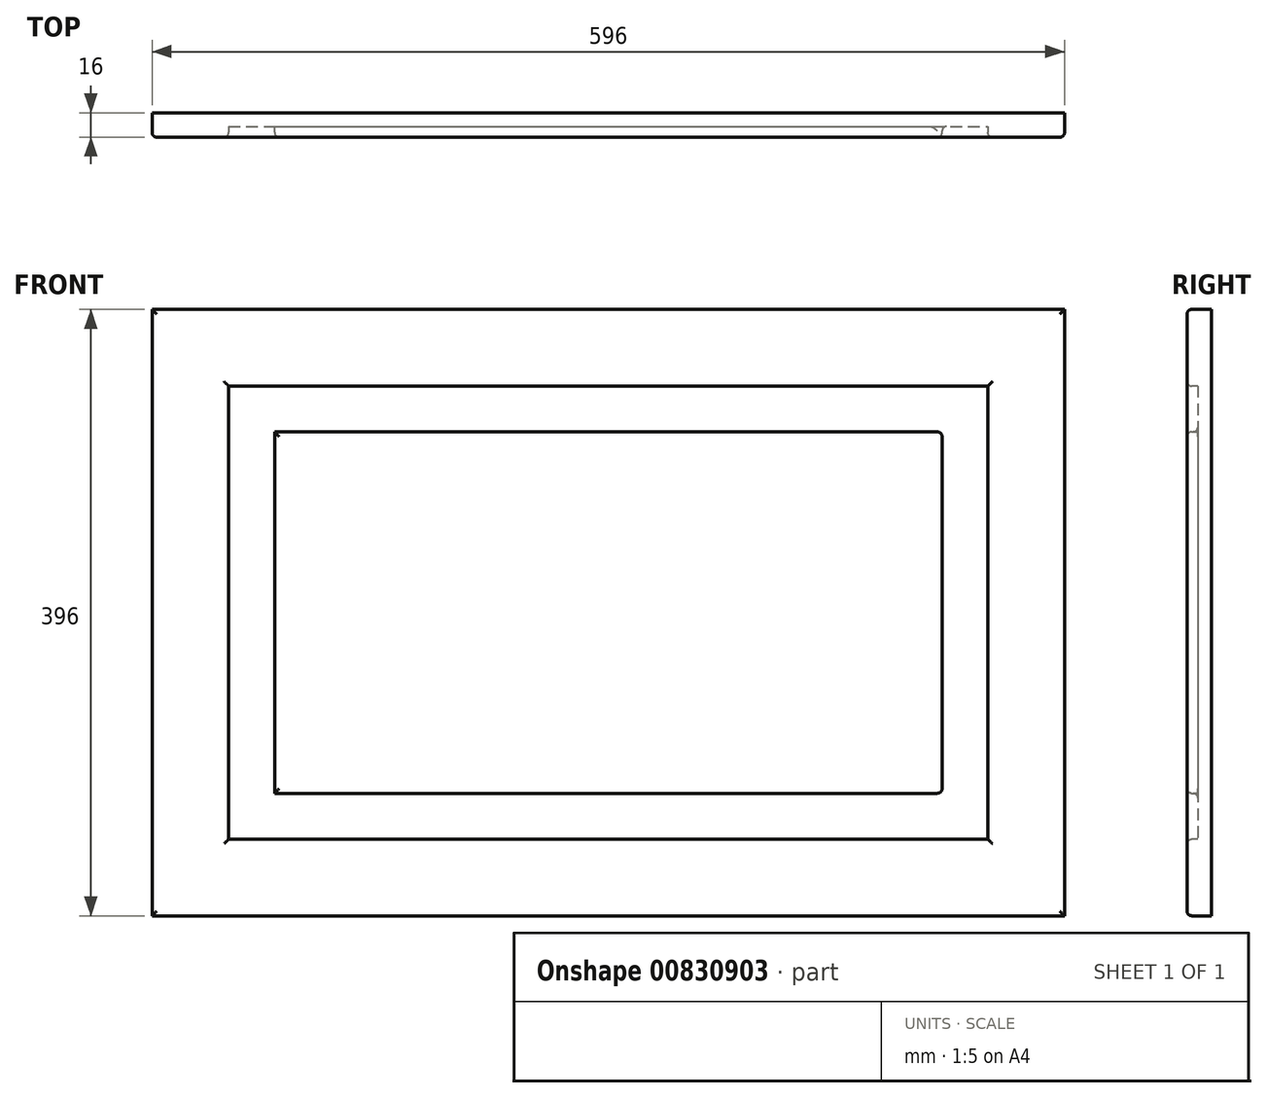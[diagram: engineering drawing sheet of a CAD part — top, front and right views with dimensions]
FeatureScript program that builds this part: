
annotation { "Feature Type Name" : "Feature", "Feature Type Description" : "" }
export const myFeature = defineFeature(function(context is Context, id is Id, definition is map)
    precondition{}
    {
        {
            var Q0;
            Q0=qCreatedBy(makeId("Front.planeOp"),FACE);
            var sketch = newSketch(context, id + "F0", { "sketchPlane" : qUnion([Q0])});
            skLineSegment(sketch, "E0.bottom", {"start": v(0, 0) * mm, "end": v(44.66, 0) * mm});
            skLineSegment(sketch, "E0.top", {"start": v(0, 33.8) * mm, "end": v(44.66, 33.8) * mm});
            skLineSegment(sketch, "E0.left", {"start": v(0, 0) * mm, "end": v(0, 33.8) * mm});
            skLineSegment(sketch, "E0.right", {"start": v(44.66, 0) * mm, "end": v(44.66, 33.8) * mm});
            skSolve(sketch);
        }
        {
            var Q0;
            Q0=makeQuery(id+"F0.imprint","IMPRINT",FACE,{"disambiguationData":[TD([[makeQuery(id+"F0.imprint","IMPRINT",EDGE,{"derivedFrom":sQuery(id+"F0.wireOp",EDGE,"E0.bottom")}),1.0]])]});
            extrude(context, id + "F1", {"entities" : qUnion([Q0]), "depth" : 16 * mm, "offsetDistance" : 25.4 * mm});
        }
        {
            var Q0;
            Q0=makeQuery(id+"F1.opExtrude","SWEPT_FACE",FACE,{"disambiguationData":[OSD([sQuery(id+"F0.wireOp",EDGE,"E0.bottom")])]});
            extrude(context, id + "F2", {"entities" : qUnion([Q0]), "operationType" : NewBodyOperationType.ADD, "oppositeDirection" : true, "depth" : 796 * mm, "offsetDistance" : 25 * mm});
        }
        {
            var Q0;
            {var subQ0=sQuery(id+"F0.wireOp",EDGE,"E0.left");Q0=makeQuery(id+"F2.boolean.opBoolean","MERGE",FACE,{"derivedFrom":[makeQuery(id+"F1.opExtrude","SWEPT_FACE",FACE,{"disambiguationData":[OSD([subQ0])]}),makeQuery(id+"F2.opExtrude","SWEPT_FACE",FACE,{"disambiguationData":[OSD([sQuery(id+"F0.wireOp",EDGE,"E0.bottom"),subQ0])]})]});}
            extrude(context, id + "F3", {"entities" : qUnion([Q0]), "operationType" : NewBodyOperationType.ADD, "oppositeDirection" : true, "depth" : 196 * mm, "offsetDistance" : 25 * mm});
        }
        {
            var Q0;
            {var subQ0=sQuery(id+"F0.wireOp",EDGE,"E0.left");var subQ1=sQuery(id+"F0.wireOp",EDGE,"E0.bottom");Q0=makeQuery(id+"F3.boolean.opBoolean","MERGE",FACE,{"derivedFrom":[makeQuery(id+"F2.boolean.opBoolean","MERGE",FACE,{"derivedFrom":[makeQuery(id+"F1.opExtrude","CAP_FACE",FACE,{"disambiguationData":[OSD([subQ1,sQuery(id+"F0.wireOp",EDGE,"E0.top"),subQ0,sQuery(id+"F0.wireOp",EDGE,"E0.right")])],"isStart":false}),makeQuery(id+"F2.opExtrude","SWEPT_FACE",FACE,{"disambiguationData":[OSD([subQ1]),TDD([makeQuery(id+"F1.opExtrude","CAP_EDGE",EDGE,{"disambiguationData":[OSD([subQ1])],"isStart":false})])]})]}),makeQuery(id+"F3.opExtrude","SWEPT_FACE",FACE,{"disambiguationData":[OSD([subQ1,subQ0]),TDD([makeQuery(id+"F2.boolean.opBoolean","MERGE",EDGE,{"derivedFrom":[makeQuery(id+"F1.opExtrude","CAP_EDGE",EDGE,{"disambiguationData":[OSD([subQ0])],"isStart":false}),makeQuery(id+"F2.opExtrude","SWEPT_EDGE",EDGE,{"disambiguationData":[OSD([subQ1,subQ0]),TDD([makeQuery(id+"F1.opExtrude","CAP_VERTEX",VERTEX,{"disambiguationData":[OSD([subQ1,subQ0])],"isStart":false})])]})]})])]})]});}
            var sketch = newSketch(context, id + "F4", { "sketchPlane" : qUnion([Q0])});
            skLineSegment(sketch, "E1.bottom", {"start": v(59.7, 646.67) * mm, "end": v(128.66, 646.67) * mm});
            skLineSegment(sketch, "E1.top", {"start": v(59.7, 152.97) * mm, "end": v(128.66, 152.97) * mm});
            skLineSegment(sketch, "E1.left", {"start": v(59.7, 646.67) * mm, "end": v(59.7, 152.97) * mm});
            skLineSegment(sketch, "E1.right", {"start": v(128.66, 646.67) * mm, "end": v(128.66, 152.97) * mm});
            skSolve(sketch);
        }
        {
            var Q0;
            Q0=makeQuery(id+"F4.imprint","IMPRINT",FACE,{"disambiguationData":[TD([[makeQuery(id+"F4.imprint","IMPRINT",EDGE,{"derivedFrom":sQuery(id+"F4.wireOp",EDGE,"E1.bottom")}),-1.0]])]});
            extrude(context, id + "F5", {"entities" : qUnion([Q0]), "operationType" : NewBodyOperationType.REMOVE, "oppositeDirection" : true, "depth" : 7 * mm, "offsetDistance" : 25 * mm});
        }
        {
            var Q0;
            Q0=makeQuery(id+"F5.boolean.opBoolean","COPY",FACE,{"derivedFrom":makeQuery(id+"F5.opExtrude","SWEPT_FACE",FACE,{"disambiguationData":[OSD([sQuery(id+"F4.wireOp",EDGE,"E1.left")])]})});
            extrude(context, id + "F6", {"entities" : qUnion([Q0]), "operationType" : NewBodyOperationType.REMOVE, "oppositeDirection" : true, "depth" : 9.7 * mm, "offsetDistance" : 25 * mm});
        }
        {
            var Q0;
            {var subQ0=sQuery(id+"F4.wireOp",EDGE,"E1.bottom");Q0=makeQuery(id+"F6.boolean.opBoolean","MERGE",FACE,{"derivedFrom":[makeQuery(id+"F5.boolean.opBoolean","COPY",FACE,{"derivedFrom":makeQuery(id+"F5.opExtrude","SWEPT_FACE",FACE,{"disambiguationData":[OSD([subQ0])]})}),makeQuery(id+"F6.opExtrude","SWEPT_FACE",FACE,{"disambiguationData":[OSD([subQ0,sQuery(id+"F4.wireOp",EDGE,"E1.left")])]})]});}
            extrude(context, id + "F7", {"entities" : qUnion([Q0]), "operationType" : NewBodyOperationType.ADD, "oppositeDirection" : true, "depth" : 99.33 * mm, "offsetDistance" : 25 * mm});
        }
        {
            var Q0;
            {var subQ0=sQuery(id+"F4.wireOp",EDGE,"E1.bottom");Q0=makeQuery(id+"F6.boolean.opBoolean","MERGE",FACE,{"derivedFrom":[makeQuery(id+"F5.boolean.opBoolean","COPY",FACE,{"derivedFrom":makeQuery(id+"F5.opExtrude","SWEPT_FACE",FACE,{"disambiguationData":[OSD([subQ0])]})}),makeQuery(id+"F6.opExtrude","SWEPT_FACE",FACE,{"disambiguationData":[OSD([subQ0,sQuery(id+"F4.wireOp",EDGE,"E1.left")])]})]});}
            extrude(context, id + "F8", {"entities" : qUnion([Q0]), "operationType" : NewBodyOperationType.REMOVE, "oppositeDirection" : true, "depth" : 99.33 * mm, "offsetDistance" : 25 * mm});
        }
        {
            var Q0;
            {var subQ0=sQuery(id+"F4.wireOp",EDGE,"E1.right");Q0=makeQuery(id+"F8.boolean.opBoolean","MERGE",FACE,{"derivedFrom":[makeQuery(id+"F5.boolean.opBoolean","COPY",FACE,{"derivedFrom":makeQuery(id+"F5.opExtrude","SWEPT_FACE",FACE,{"disambiguationData":[OSD([subQ0])]})}),makeQuery(id+"F8.opExtrude","SWEPT_FACE",FACE,{"disambiguationData":[OSD([sQuery(id+"F4.wireOp",EDGE,"E1.bottom"),subQ0])]})]});}
            extrude(context, id + "F9", {"entities" : qUnion([Q0]), "operationType" : NewBodyOperationType.REMOVE, "oppositeDirection" : true, "depth" : 17.34 * mm, "offsetDistance" : 25 * mm});
        }
        {
            var Q0;
            {var subQ0=sQuery(id+"F4.wireOp",EDGE,"E1.top");Q0=makeQuery(id+"F9.boolean.opBoolean","MERGE",FACE,{"derivedFrom":[makeQuery(id+"F6.boolean.opBoolean","MERGE",FACE,{"derivedFrom":[makeQuery(id+"F5.boolean.opBoolean","COPY",FACE,{"derivedFrom":makeQuery(id+"F5.opExtrude","SWEPT_FACE",FACE,{"disambiguationData":[OSD([subQ0])]})}),makeQuery(id+"F6.opExtrude","SWEPT_FACE",FACE,{"disambiguationData":[OSD([subQ0,sQuery(id+"F4.wireOp",EDGE,"E1.left")])]})]}),makeQuery(id+"F9.opExtrude","SWEPT_FACE",FACE,{"disambiguationData":[OSD([subQ0,sQuery(id+"F4.wireOp",EDGE,"E1.right")])]})]});}
            extrude(context, id + "F10", {"entities" : qUnion([Q0]), "operationType" : NewBodyOperationType.REMOVE, "oppositeDirection" : true, "depth" : 102.97 * mm, "offsetDistance" : 25 * mm});
        }
        {
            var Q0;
            {var subQ0=sQuery(id+"F4.wireOp",EDGE,"E1.right");var subQ1=sQuery(id+"F4.wireOp",EDGE,"E1.top");var subQ2=sQuery(id+"F4.wireOp",EDGE,"E1.left");var subQ3=sQuery(id+"F4.wireOp",EDGE,"E1.bottom");Q0=makeQuery(id+"F10.boolean.opBoolean","MERGE",FACE,{"derivedFrom":[makeQuery(id+"F9.boolean.opBoolean","MERGE",FACE,{"derivedFrom":[makeQuery(id+"F8.boolean.opBoolean","MERGE",FACE,{"derivedFrom":[makeQuery(id+"F6.boolean.opBoolean","MERGE",FACE,{"derivedFrom":[makeQuery(id+"F5.boolean.opBoolean","COPY",FACE,{"derivedFrom":makeQuery(id+"F5.opExtrude","CAP_FACE",FACE,{"disambiguationData":[OSD([subQ3,subQ1,subQ2,subQ0])],"isStart":false})}),makeQuery(id+"F6.opExtrude","SWEPT_FACE",FACE,{"disambiguationData":[OSD([subQ2]),TDD([makeQuery(id+"F5.boolean.opBoolean","COPY",EDGE,{"derivedFrom":makeQuery(id+"F5.opExtrude","CAP_EDGE",EDGE,{"disambiguationData":[OSD([subQ2])],"isStart":false})})])]})]}),makeQuery(id+"F8.opExtrude","SWEPT_FACE",FACE,{"disambiguationData":[OSD([subQ3,subQ2]),TDD([makeQuery(id+"F6.boolean.opBoolean","MERGE",EDGE,{"derivedFrom":[makeQuery(id+"F5.boolean.opBoolean","COPY",EDGE,{"derivedFrom":makeQuery(id+"F5.opExtrude","CAP_EDGE",EDGE,{"disambiguationData":[OSD([subQ3])],"isStart":false})}),makeQuery(id+"F6.opExtrude","SWEPT_EDGE",EDGE,{"disambiguationData":[OSD([subQ3,subQ2]),TDD([makeQuery(id+"F5.boolean.opBoolean","COPY",VERTEX,{"derivedFrom":makeQuery(id+"F5.opExtrude","CAP_VERTEX",VERTEX,{"disambiguationData":[OSD([subQ3,subQ2])],"isStart":false})})])]})]})])]})]}),makeQuery(id+"F9.opExtrude","SWEPT_FACE",FACE,{"disambiguationData":[OSD([subQ3,subQ0]),TDD([makeQuery(id+"F8.boolean.opBoolean","MERGE",EDGE,{"derivedFrom":[makeQuery(id+"F5.boolean.opBoolean","COPY",EDGE,{"derivedFrom":makeQuery(id+"F5.opExtrude","CAP_EDGE",EDGE,{"disambiguationData":[OSD([subQ0])],"isStart":false})}),makeQuery(id+"F8.opExtrude","SWEPT_EDGE",EDGE,{"disambiguationData":[OSD([subQ3,subQ0]),TDD([makeQuery(id+"F5.boolean.opBoolean","COPY",VERTEX,{"derivedFrom":makeQuery(id+"F5.opExtrude","CAP_VERTEX",VERTEX,{"disambiguationData":[OSD([subQ3,subQ0])],"isStart":false})})])]})]})])]})]}),makeQuery(id+"F10.opExtrude","SWEPT_FACE",FACE,{"disambiguationData":[OSD([subQ1,subQ2,subQ0]),TDD([makeQuery(id+"F9.boolean.opBoolean","MERGE",EDGE,{"derivedFrom":[makeQuery(id+"F6.boolean.opBoolean","MERGE",EDGE,{"derivedFrom":[makeQuery(id+"F5.boolean.opBoolean","COPY",EDGE,{"derivedFrom":makeQuery(id+"F5.opExtrude","CAP_EDGE",EDGE,{"disambiguationData":[OSD([subQ1])],"isStart":false})}),makeQuery(id+"F6.opExtrude","SWEPT_EDGE",EDGE,{"disambiguationData":[OSD([subQ1,subQ2]),TDD([makeQuery(id+"F5.boolean.opBoolean","COPY",VERTEX,{"derivedFrom":makeQuery(id+"F5.opExtrude","CAP_VERTEX",VERTEX,{"disambiguationData":[OSD([subQ1,subQ2])],"isStart":false})})])]})]}),makeQuery(id+"F9.opExtrude","SWEPT_EDGE",EDGE,{"disambiguationData":[OSD([subQ1,subQ0]),TDD([makeQuery(id+"F5.boolean.opBoolean","COPY",VERTEX,{"derivedFrom":makeQuery(id+"F5.opExtrude","CAP_VERTEX",VERTEX,{"disambiguationData":[OSD([subQ1,subQ0])],"isStart":false})})])]})]})])]})]});}
            var sketch = newSketch(context, id + "F11", { "sketchPlane" : qUnion([Q0])});
            skLineSegment(sketch, "E2.bottom", {"start": v(74.13, 678.73) * mm, "end": v(109.41, 678.73) * mm});
            skLineSegment(sketch, "E2.top", {"start": v(74.13, 186.63) * mm, "end": v(109.41, 186.63) * mm});
            skLineSegment(sketch, "E2.left", {"start": v(74.13, 678.73) * mm, "end": v(74.13, 186.63) * mm});
            skLineSegment(sketch, "E2.right", {"start": v(109.41, 678.73) * mm, "end": v(109.41, 186.63) * mm});
            skSolve(sketch);
        }
        {
            var Q0;
            Q0=makeQuery(id+"F11.imprint","IMPRINT",FACE,{"disambiguationData":[TD([[makeQuery(id+"F11.imprint","IMPRINT",EDGE,{"derivedFrom":sQuery(id+"F11.wireOp",EDGE,"E2.bottom")}),-1.0]])]});
            extrude(context, id + "F12", {"entities" : qUnion([Q0]), "operationType" : NewBodyOperationType.ADD, "depth" : 7 * mm, "offsetDistance" : 25 * mm});
        }
        {
            var Q0;
            Q0=makeQuery(id+"F12.opExtrude","SWEPT_FACE",FACE,{"disambiguationData":[OSD([sQuery(id+"F11.wireOp",EDGE,"E2.bottom")])]});
            extrude(context, id + "F13", {"entities" : qUnion([Q0]), "operationType" : NewBodyOperationType.ADD, "depth" : 37.27 * mm, "offsetDistance" : 25 * mm});
        }
        {
            var Q0;
            {var subQ0=sQuery(id+"F11.wireOp",EDGE,"E2.right");Q0=makeQuery(id+"F13.boolean.opBoolean","MERGE",FACE,{"derivedFrom":[makeQuery(id+"F12.opExtrude","SWEPT_FACE",FACE,{"disambiguationData":[OSD([subQ0])]}),makeQuery(id+"F13.opExtrude","SWEPT_FACE",FACE,{"disambiguationData":[OSD([sQuery(id+"F11.wireOp",EDGE,"E2.bottom"),subQ0])]})]});}
            extrude(context, id + "F14", {"entities" : qUnion([Q0]), "operationType" : NewBodyOperationType.ADD, "depth" : 6.58 * mm, "offsetDistance" : 25 * mm});
        }
        {
            var Q0;
            {var subQ0=sQuery(id+"F11.wireOp",EDGE,"E2.top");Q0=makeQuery(id+"F14.boolean.opBoolean","MERGE",FACE,{"derivedFrom":[makeQuery(id+"F12.opExtrude","SWEPT_FACE",FACE,{"disambiguationData":[OSD([subQ0])]}),makeQuery(id+"F14.opExtrude","SWEPT_FACE",FACE,{"disambiguationData":[OSD([subQ0,sQuery(id+"F11.wireOp",EDGE,"E2.right")])]})]});}
            extrude(context, id + "F15", {"entities" : qUnion([Q0]), "operationType" : NewBodyOperationType.ADD, "depth" : 106.63 * mm, "offsetDistance" : 25 * mm});
        }
        {
            var Q0;
            {var subQ0=sQuery(id+"F11.wireOp",EDGE,"E2.left");Q0=makeQuery(id+"F15.boolean.opBoolean","MERGE",FACE,{"derivedFrom":[makeQuery(id+"F13.boolean.opBoolean","MERGE",FACE,{"derivedFrom":[makeQuery(id+"F12.opExtrude","SWEPT_FACE",FACE,{"disambiguationData":[OSD([subQ0])]}),makeQuery(id+"F13.opExtrude","SWEPT_FACE",FACE,{"disambiguationData":[OSD([sQuery(id+"F11.wireOp",EDGE,"E2.bottom"),subQ0])]})]}),makeQuery(id+"F15.opExtrude","SWEPT_FACE",FACE,{"disambiguationData":[OSD([sQuery(id+"F11.wireOp",EDGE,"E2.top"),subQ0])]})]});}
            extrude(context, id + "F16", {"entities" : qUnion([Q0]), "operationType" : NewBodyOperationType.REMOVE, "oppositeDirection" : true, "depth" : 5.87 * mm, "offsetDistance" : 25 * mm});
        }
        {
            var Q0;
            Q0=makeQuery(id+"F3.opExtrude","CAP_FACE",FACE,{"disambiguationData":[OSD([sQuery(id+"F0.wireOp",EDGE,"E0.bottom"),sQuery(id+"F0.wireOp",EDGE,"E0.left")])],"isStart":false});
            extrude(context, id + "F17", {"entities" : qUnion([Q0]), "operationType" : NewBodyOperationType.ADD, "depth" : 200 * mm, "offsetDistance" : 25 * mm});
        }
        {
            var Q0;
            {var subQ0=sQuery(id+"F4.wireOp",EDGE,"E1.right");Q0=makeQuery(id+"F10.boolean.opBoolean","MERGE",FACE,{"derivedFrom":[makeQuery(id+"F9.boolean.opBoolean","COPY",FACE,{"derivedFrom":makeQuery(id+"F9.opExtrude","CAP_FACE",FACE,{"disambiguationData":[OSD([sQuery(id+"F4.wireOp",EDGE,"E1.bottom"),subQ0])],"isStart":false})}),makeQuery(id+"F10.opExtrude","SWEPT_FACE",FACE,{"disambiguationData":[OSD([sQuery(id+"F4.wireOp",EDGE,"E1.top"),subQ0])]})]});}
            extrude(context, id + "F18", {"entities" : qUnion([Q0]), "operationType" : NewBodyOperationType.REMOVE, "oppositeDirection" : true, "depth" : 200 * mm, "offsetDistance" : 25 * mm});
        }
        {
            var Q0;
            {var subQ0=sQuery(id+"F11.wireOp",EDGE,"E2.right");var subQ1=sQuery(id+"F11.wireOp",EDGE,"E2.top");Q0=makeQuery(id+"F15.boolean.opBoolean","MERGE",FACE,{"derivedFrom":[makeQuery(id+"F14.opExtrude","CAP_FACE",FACE,{"disambiguationData":[OSD([sQuery(id+"F11.wireOp",EDGE,"E2.bottom"),subQ0])],"isStart":false}),makeQuery(id+"F15.opExtrude","SWEPT_FACE",FACE,{"disambiguationData":[OSD([subQ1,subQ0]),TDD([makeQuery(id+"F14.opExtrude","CAP_EDGE",EDGE,{"disambiguationData":[OSD([subQ1,subQ0])],"isStart":false})])]})]});}
            extrude(context, id + "F19", {"entities" : qUnion([Q0]), "operationType" : NewBodyOperationType.ADD, "depth" : 200 * mm, "offsetDistance" : 25 * mm});
        }
        {
            var Q0;
            Q0=makeQuery(id+"F17.opExtrude","CAP_FACE",FACE,{"disambiguationData":[OSD([sQuery(id+"F0.wireOp",EDGE,"E0.bottom"),sQuery(id+"F0.wireOp",EDGE,"E0.left")])],"isStart":false});
            extrude(context, id + "F20", {"entities" : qUnion([Q0]), "operationType" : NewBodyOperationType.ADD, "depth" : 200 * mm, "offsetDistance" : 25 * mm});
        }
        {
            var Q0;
            Q0=makeQuery(id+"F18.boolean.opBoolean","COPY",FACE,{"derivedFrom":makeQuery(id+"F18.opExtrude","CAP_FACE",FACE,{"disambiguationData":[OSD([sQuery(id+"F4.wireOp",EDGE,"E1.bottom"),sQuery(id+"F4.wireOp",EDGE,"E1.top"),sQuery(id+"F4.wireOp",EDGE,"E1.right")])],"isStart":false})});
            extrude(context, id + "F21", {"entities" : qUnion([Q0]), "operationType" : NewBodyOperationType.REMOVE, "oppositeDirection" : true, "depth" : 200 * mm, "offsetDistance" : 25 * mm});
        }
        {
            var Q0;
            Q0=makeQuery(id+"F19.opExtrude","CAP_FACE",FACE,{"disambiguationData":[OSD([sQuery(id+"F11.wireOp",EDGE,"E2.bottom"),sQuery(id+"F11.wireOp",EDGE,"E2.top"),sQuery(id+"F11.wireOp",EDGE,"E2.right")])],"isStart":false});
            extrude(context, id + "F22", {"entities" : qUnion([Q0]), "operationType" : NewBodyOperationType.ADD, "depth" : 200 * mm, "offsetDistance" : 25 * mm});
        }
        {
            var Q0;
            {var subQ0=sQuery(id+"F11.wireOp",EDGE,"E2.right");var subQ1=sQuery(id+"F11.wireOp",EDGE,"E2.top");Q0=makeQuery(id+"F22.boolean.opBoolean","MERGE",FACE,{"derivedFrom":[makeQuery(id+"F19.boolean.opBoolean","MERGE",FACE,{"derivedFrom":[makeQuery(id+"F15.opExtrude","CAP_FACE",FACE,{"disambiguationData":[OSD([subQ1,subQ0])],"isStart":false}),makeQuery(id+"F19.opExtrude","SWEPT_FACE",FACE,{"disambiguationData":[OSD([subQ1,subQ0])]})]}),makeQuery(id+"F22.opExtrude","SWEPT_FACE",FACE,{"disambiguationData":[OSD([subQ1,subQ0])]})]});}
            extrude(context, id + "F23", {"entities" : qUnion([Q0]), "operationType" : NewBodyOperationType.REMOVE, "oppositeDirection" : true, "depth" : 600 * mm, "offsetDistance" : 25 * mm});
        }
        {
            var Q0;
            {var subQ0=sQuery(id+"F4.wireOp",EDGE,"E1.right");var subQ1=sQuery(id+"F4.wireOp",EDGE,"E1.top");Q0=makeQuery(id+"F21.boolean.opBoolean","MERGE",FACE,{"derivedFrom":[makeQuery(id+"F18.boolean.opBoolean","MERGE",FACE,{"derivedFrom":[makeQuery(id+"F10.boolean.opBoolean","COPY",FACE,{"derivedFrom":makeQuery(id+"F10.opExtrude","CAP_FACE",FACE,{"disambiguationData":[OSD([subQ1,sQuery(id+"F4.wireOp",EDGE,"E1.left"),subQ0])],"isStart":false})}),makeQuery(id+"F18.opExtrude","SWEPT_FACE",FACE,{"disambiguationData":[OSD([subQ1,subQ0])]})]}),makeQuery(id+"F21.opExtrude","SWEPT_FACE",FACE,{"disambiguationData":[OSD([subQ1,subQ0])]})]});}
            extrude(context, id + "F24", {"entities" : qUnion([Q0]), "operationType" : NewBodyOperationType.ADD, "depth" : 600 * mm, "offsetDistance" : 25 * mm});
        }
        {
            var Q0;
            {var subQ0=sQuery(id+"F0.wireOp",EDGE,"E0.left");var subQ1=sQuery(id+"F0.wireOp",EDGE,"E0.bottom");var subQ2=makeQuery(id+"F1.opExtrude","SWEPT_EDGE",EDGE,{"disambiguationData":[OSD([subQ1,subQ0])]});var subQ3=makeQuery(id+"F3.opExtrude","CAP_EDGE",EDGE,{"disambiguationData":[OSD([subQ1,subQ0]),TDD([subQ2])],"isStart":false});Q0=makeQuery(id+"F20.boolean.opBoolean","MERGE",FACE,{"derivedFrom":[makeQuery(id+"F17.boolean.opBoolean","MERGE",FACE,{"derivedFrom":[makeQuery(id+"F3.boolean.opBoolean","MERGE",FACE,{"derivedFrom":[makeQuery(id+"F1.opExtrude","SWEPT_FACE",FACE,{"disambiguationData":[OSD([subQ1])]}),makeQuery(id+"F3.opExtrude","SWEPT_FACE",FACE,{"disambiguationData":[OSD([subQ1,subQ0]),TDD([subQ2])]})]}),makeQuery(id+"F17.opExtrude","SWEPT_FACE",FACE,{"disambiguationData":[OSD([subQ1,subQ0]),TDD([subQ3])]})]}),makeQuery(id+"F20.opExtrude","SWEPT_FACE",FACE,{"disambiguationData":[OSD([subQ1,subQ0]),TDD([makeQuery(id+"F17.opExtrude","CAP_EDGE",EDGE,{"disambiguationData":[OSD([subQ1,subQ0]),TDD([subQ3])],"isStart":false})])]})]});}
            extrude(context, id + "F25", {"entities" : qUnion([Q0]), "operationType" : NewBodyOperationType.REMOVE, "oppositeDirection" : true, "depth" : 600 * mm, "offsetDistance" : 25 * mm});
        }
        {
            var Q0;
            Q0=makeQuery(id+"F25.boolean.opBoolean","COPY",FACE,{"derivedFrom":makeQuery(id+"F25.opExtrude","CAP_FACE",FACE,{"disambiguationData":[OSD([sQuery(id+"F0.wireOp",EDGE,"E0.bottom"),sQuery(id+"F0.wireOp",EDGE,"E0.left")])],"isStart":false})});
            extrude(context, id + "F26", {"entities" : qUnion([Q0]), "operationType" : NewBodyOperationType.ADD, "depth" : 200 * mm, "offsetDistance" : 25 * mm});
        }
        {
            var Q0;
            Q0=makeQuery(id+"F24.opExtrude","CAP_FACE",FACE,{"disambiguationData":[OSD([sQuery(id+"F4.wireOp",EDGE,"E1.top"),sQuery(id+"F4.wireOp",EDGE,"E1.left"),sQuery(id+"F4.wireOp",EDGE,"E1.right")])],"isStart":false});
            extrude(context, id + "F27", {"entities" : qUnion([Q0]), "operationType" : NewBodyOperationType.REMOVE, "oppositeDirection" : true, "depth" : 200 * mm, "offsetDistance" : 25 * mm});
        }
        {
            var Q0;
            Q0=makeQuery(id+"F23.boolean.opBoolean","COPY",FACE,{"derivedFrom":makeQuery(id+"F23.opExtrude","CAP_FACE",FACE,{"disambiguationData":[OSD([sQuery(id+"F11.wireOp",EDGE,"E2.top"),sQuery(id+"F11.wireOp",EDGE,"E2.right")])],"isStart":false})});
            extrude(context, id + "F28", {"entities" : qUnion([Q0]), "operationType" : NewBodyOperationType.ADD, "depth" : 200 * mm, "offsetDistance" : 25 * mm});
        }
        {
            var Q0;
            {var subQ0=sQuery(id+"F11.wireOp",EDGE,"E2.right");var subQ1=sQuery(id+"F11.wireOp",EDGE,"E2.top");var subQ2=makeQuery(id+"F12.opExtrude","CAP_VERTEX",VERTEX,{"disambiguationData":[OSD([subQ1,subQ0])],"isStart":false});var subQ3=makeQuery(id+"F14.opExtrude","CAP_VERTEX",VERTEX,{"disambiguationData":[OSD([subQ1,subQ0]),TDD([subQ2])],"isStart":false});var subQ4=makeQuery(id+"F15.opExtrude","CAP_VERTEX",VERTEX,{"disambiguationData":[OSD([subQ1,subQ0]),TDD([subQ3])],"isStart":false});var subQ5=makeQuery(id+"F14.boolean.opBoolean","MERGE",EDGE,{"derivedFrom":[makeQuery(id+"F12.opExtrude","CAP_EDGE",EDGE,{"disambiguationData":[OSD([subQ1])],"isStart":false}),makeQuery(id+"F14.opExtrude","SWEPT_EDGE",EDGE,{"disambiguationData":[OSD([subQ1,subQ0]),TDD([subQ2])]})]});var subQ6=sQuery(id+"F11.wireOp",EDGE,"E2.bottom");var subQ7=makeQuery(id+"F13.boolean.opBoolean","MERGE",EDGE,{"derivedFrom":[makeQuery(id+"F12.opExtrude","CAP_EDGE",EDGE,{"disambiguationData":[OSD([subQ0])],"isStart":false}),makeQuery(id+"F13.opExtrude","SWEPT_EDGE",EDGE,{"disambiguationData":[OSD([subQ6,subQ0]),TDD([makeQuery(id+"F12.opExtrude","CAP_VERTEX",VERTEX,{"disambiguationData":[OSD([subQ6,subQ0])],"isStart":false})])]})]});var subQ8=makeQuery(id+"F15.boolean.opBoolean","MERGE",EDGE,{"derivedFrom":[makeQuery(id+"F14.opExtrude","CAP_EDGE",EDGE,{"disambiguationData":[OSD([subQ6,subQ0]),TDD([subQ7])],"isStart":false}),makeQuery(id+"F15.opExtrude","SWEPT_EDGE",EDGE,{"disambiguationData":[OSD([subQ1,subQ0]),TDD([subQ3])]})]});Q0=makeQuery(id+"F28.boolean.opBoolean","MERGE",FACE,{"derivedFrom":[makeQuery(id+"F22.boolean.opBoolean","MERGE",FACE,{"derivedFrom":[makeQuery(id+"F19.boolean.opBoolean","MERGE",FACE,{"derivedFrom":[makeQuery(id+"F15.boolean.opBoolean","MERGE",FACE,{"derivedFrom":[makeQuery(id+"F14.boolean.opBoolean","MERGE",FACE,{"derivedFrom":[makeQuery(id+"F13.boolean.opBoolean","MERGE",FACE,{"derivedFrom":[makeQuery(id+"F12.opExtrude","CAP_FACE",FACE,{"disambiguationData":[OSD([subQ6,subQ1,sQuery(id+"F11.wireOp",EDGE,"E2.left"),subQ0])],"isStart":false}),makeQuery(id+"F13.opExtrude","SWEPT_FACE",FACE,{"disambiguationData":[OSD([subQ6]),TDD([makeQuery(id+"F12.opExtrude","CAP_EDGE",EDGE,{"disambiguationData":[OSD([subQ6])],"isStart":false})])]})]}),makeQuery(id+"F14.opExtrude","SWEPT_FACE",FACE,{"disambiguationData":[OSD([subQ6,subQ0]),TDD([subQ7])]})]}),makeQuery(id+"F15.opExtrude","SWEPT_FACE",FACE,{"disambiguationData":[OSD([subQ1,subQ0]),TDD([subQ5])]})]}),makeQuery(id+"F19.opExtrude","SWEPT_FACE",FACE,{"disambiguationData":[OSD([subQ6,subQ1,subQ0]),TDD([subQ8])]})]}),makeQuery(id+"F22.opExtrude","SWEPT_FACE",FACE,{"disambiguationData":[OSD([subQ6,subQ1,subQ0]),TDD([makeQuery(id+"F19.opExtrude","CAP_EDGE",EDGE,{"disambiguationData":[OSD([subQ6,subQ1,subQ0]),TDD([subQ8])],"isStart":false})])]})]}),makeQuery(id+"F28.opExtrude","SWEPT_FACE",FACE,{"disambiguationData":[OSD([subQ1,subQ0]),TDD([makeQuery(id+"F23.boolean.opBoolean","COPY",EDGE,{"derivedFrom":makeQuery(id+"F23.opExtrude","CAP_EDGE",EDGE,{"disambiguationData":[OSD([subQ1,subQ0]),TDD([makeQuery(id+"F22.boolean.opBoolean","MERGE",EDGE,{"derivedFrom":[makeQuery(id+"F19.boolean.opBoolean","MERGE",EDGE,{"derivedFrom":[makeQuery(id+"F15.opExtrude","CAP_EDGE",EDGE,{"disambiguationData":[OSD([subQ1,subQ0]),TDD([subQ5])],"isStart":false}),makeQuery(id+"F19.opExtrude","SWEPT_EDGE",EDGE,{"disambiguationData":[OSD([subQ1,subQ0]),TDD([subQ4])]})]}),makeQuery(id+"F22.opExtrude","SWEPT_EDGE",EDGE,{"disambiguationData":[OSD([subQ1,subQ0]),TDD([makeQuery(id+"F19.opExtrude","CAP_VERTEX",VERTEX,{"disambiguationData":[OSD([subQ1,subQ0]),TDD([subQ4])],"isStart":false})])]})]})])],"isStart":false})})])]})]});}
            var Q1;
            {var subQ0=sQuery(id+"F0.wireOp",EDGE,"E0.left");var subQ1=sQuery(id+"F0.wireOp",EDGE,"E0.bottom");var subQ2=makeQuery(id+"F1.opExtrude","CAP_VERTEX",VERTEX,{"disambiguationData":[OSD([subQ1,subQ0])],"isStart":false});var subQ3=makeQuery(id+"F3.opExtrude","CAP_VERTEX",VERTEX,{"disambiguationData":[OSD([subQ1,subQ0]),TDD([subQ2])],"isStart":false});var subQ4=makeQuery(id+"F1.opExtrude","CAP_EDGE",EDGE,{"disambiguationData":[OSD([subQ1])],"isStart":false});var subQ5=sQuery(id+"F4.wireOp",EDGE,"E1.right");var subQ6=sQuery(id+"F4.wireOp",EDGE,"E1.top");var subQ7=makeQuery(id+"F5.boolean.opBoolean","COPY",VERTEX,{"derivedFrom":makeQuery(id+"F5.opExtrude","CAP_VERTEX",VERTEX,{"disambiguationData":[OSD([subQ6,subQ5])],"isStart":true})});var subQ8=makeQuery(id+"F10.boolean.opBoolean","COPY",VERTEX,{"derivedFrom":makeQuery(id+"F10.opExtrude","CAP_VERTEX",VERTEX,{"disambiguationData":[OSD([subQ6,subQ5]),TDD([makeQuery(id+"F9.boolean.opBoolean","COPY",VERTEX,{"derivedFrom":makeQuery(id+"F9.opExtrude","CAP_VERTEX",VERTEX,{"disambiguationData":[OSD([subQ6,subQ5]),TDD([subQ7])],"isStart":false})})])],"isStart":false})});var subQ9=sQuery(id+"F4.wireOp",EDGE,"E1.left");var subQ10=makeQuery(id+"F2.boolean.opBoolean","MERGE",EDGE,{"derivedFrom":[makeQuery(id+"F1.opExtrude","CAP_EDGE",EDGE,{"disambiguationData":[OSD([subQ0])],"isStart":false}),makeQuery(id+"F2.opExtrude","SWEPT_EDGE",EDGE,{"disambiguationData":[OSD([subQ1,subQ0]),TDD([subQ2])]})]});var subQ11=makeQuery(id+"F3.opExtrude","CAP_EDGE",EDGE,{"disambiguationData":[OSD([subQ1,subQ0]),TDD([subQ10])],"isStart":false});Q1=makeQuery(id+"F26.boolean.opBoolean","MERGE",FACE,{"derivedFrom":[makeQuery(id+"F24.boolean.opBoolean","MERGE",FACE,{"derivedFrom":[makeQuery(id+"F20.boolean.opBoolean","MERGE",FACE,{"derivedFrom":[makeQuery(id+"F17.boolean.opBoolean","MERGE",FACE,{"derivedFrom":[makeQuery(id+"F3.boolean.opBoolean","MERGE",FACE,{"derivedFrom":[makeQuery(id+"F2.boolean.opBoolean","MERGE",FACE,{"derivedFrom":[makeQuery(id+"F1.opExtrude","CAP_FACE",FACE,{"disambiguationData":[OSD([subQ1,sQuery(id+"F0.wireOp",EDGE,"E0.top"),subQ0,sQuery(id+"F0.wireOp",EDGE,"E0.right")])],"isStart":false}),makeQuery(id+"F2.opExtrude","SWEPT_FACE",FACE,{"disambiguationData":[OSD([subQ1]),TDD([subQ4])]})]}),makeQuery(id+"F3.opExtrude","SWEPT_FACE",FACE,{"disambiguationData":[OSD([subQ1,subQ0]),TDD([subQ10])]})]}),makeQuery(id+"F17.opExtrude","SWEPT_FACE",FACE,{"disambiguationData":[OSD([subQ1,subQ0]),TDD([subQ11])]})]}),makeQuery(id+"F20.opExtrude","SWEPT_FACE",FACE,{"disambiguationData":[OSD([subQ1,subQ0]),TDD([makeQuery(id+"F17.opExtrude","CAP_EDGE",EDGE,{"disambiguationData":[OSD([subQ1,subQ0]),TDD([subQ11])],"isStart":false})])]})]}),makeQuery(id+"F24.opExtrude","SWEPT_FACE",FACE,{"disambiguationData":[OSD([subQ6,subQ9,subQ5]),TDD([makeQuery(id+"F21.boolean.opBoolean","MERGE",EDGE,{"derivedFrom":[makeQuery(id+"F18.boolean.opBoolean","MERGE",EDGE,{"derivedFrom":[makeQuery(id+"F10.boolean.opBoolean","COPY",EDGE,{"derivedFrom":makeQuery(id+"F10.opExtrude","CAP_EDGE",EDGE,{"disambiguationData":[OSD([subQ6,subQ9,subQ5]),TDD([makeQuery(id+"F9.boolean.opBoolean","MERGE",EDGE,{"derivedFrom":[makeQuery(id+"F6.boolean.opBoolean","MERGE",EDGE,{"derivedFrom":[makeQuery(id+"F5.boolean.opBoolean","COPY",EDGE,{"derivedFrom":makeQuery(id+"F5.opExtrude","CAP_EDGE",EDGE,{"disambiguationData":[OSD([subQ6])],"isStart":true})}),makeQuery(id+"F6.opExtrude","SWEPT_EDGE",EDGE,{"disambiguationData":[OSD([subQ6,subQ9]),TDD([makeQuery(id+"F5.boolean.opBoolean","COPY",VERTEX,{"derivedFrom":makeQuery(id+"F5.opExtrude","CAP_VERTEX",VERTEX,{"disambiguationData":[OSD([subQ6,subQ9])],"isStart":true})})])]})]}),makeQuery(id+"F9.opExtrude","SWEPT_EDGE",EDGE,{"disambiguationData":[OSD([subQ6,subQ5]),TDD([subQ7])]})]})])],"isStart":false})}),makeQuery(id+"F18.opExtrude","SWEPT_EDGE",EDGE,{"disambiguationData":[OSD([subQ6,subQ5]),TDD([subQ8])]})]}),makeQuery(id+"F21.opExtrude","SWEPT_EDGE",EDGE,{"disambiguationData":[OSD([subQ6,subQ5]),TDD([makeQuery(id+"F18.boolean.opBoolean","COPY",VERTEX,{"derivedFrom":makeQuery(id+"F18.opExtrude","CAP_VERTEX",VERTEX,{"disambiguationData":[OSD([subQ6,subQ5]),TDD([subQ8])],"isStart":false})})])]})]})])]})]}),makeQuery(id+"F26.opExtrude","SWEPT_FACE",FACE,{"disambiguationData":[OSD([subQ1,subQ0]),TDD([makeQuery(id+"F25.boolean.opBoolean","COPY",EDGE,{"derivedFrom":makeQuery(id+"F25.opExtrude","CAP_EDGE",EDGE,{"disambiguationData":[OSD([subQ1,subQ0]),TDD([makeQuery(id+"F20.boolean.opBoolean","MERGE",EDGE,{"derivedFrom":[makeQuery(id+"F17.boolean.opBoolean","MERGE",EDGE,{"derivedFrom":[makeQuery(id+"F3.boolean.opBoolean","MERGE",EDGE,{"derivedFrom":[subQ4,makeQuery(id+"F3.opExtrude","SWEPT_EDGE",EDGE,{"disambiguationData":[OSD([subQ1,subQ0]),TDD([subQ2])]})]}),makeQuery(id+"F17.opExtrude","SWEPT_EDGE",EDGE,{"disambiguationData":[OSD([subQ1,subQ0]),TDD([subQ3])]})]}),makeQuery(id+"F20.opExtrude","SWEPT_EDGE",EDGE,{"disambiguationData":[OSD([subQ1,subQ0]),TDD([makeQuery(id+"F17.opExtrude","CAP_VERTEX",VERTEX,{"disambiguationData":[OSD([subQ1,subQ0]),TDD([subQ3])],"isStart":false})])]})]})])],"isStart":false})})])]})]});}
            fillet(context, id + "F29", {"entities" : qUnion([Q0, Q1]), "radius" : 3 * mm, "tangentPropagation" : true, "allowEdgeOverflow" : false});
        }
    });
